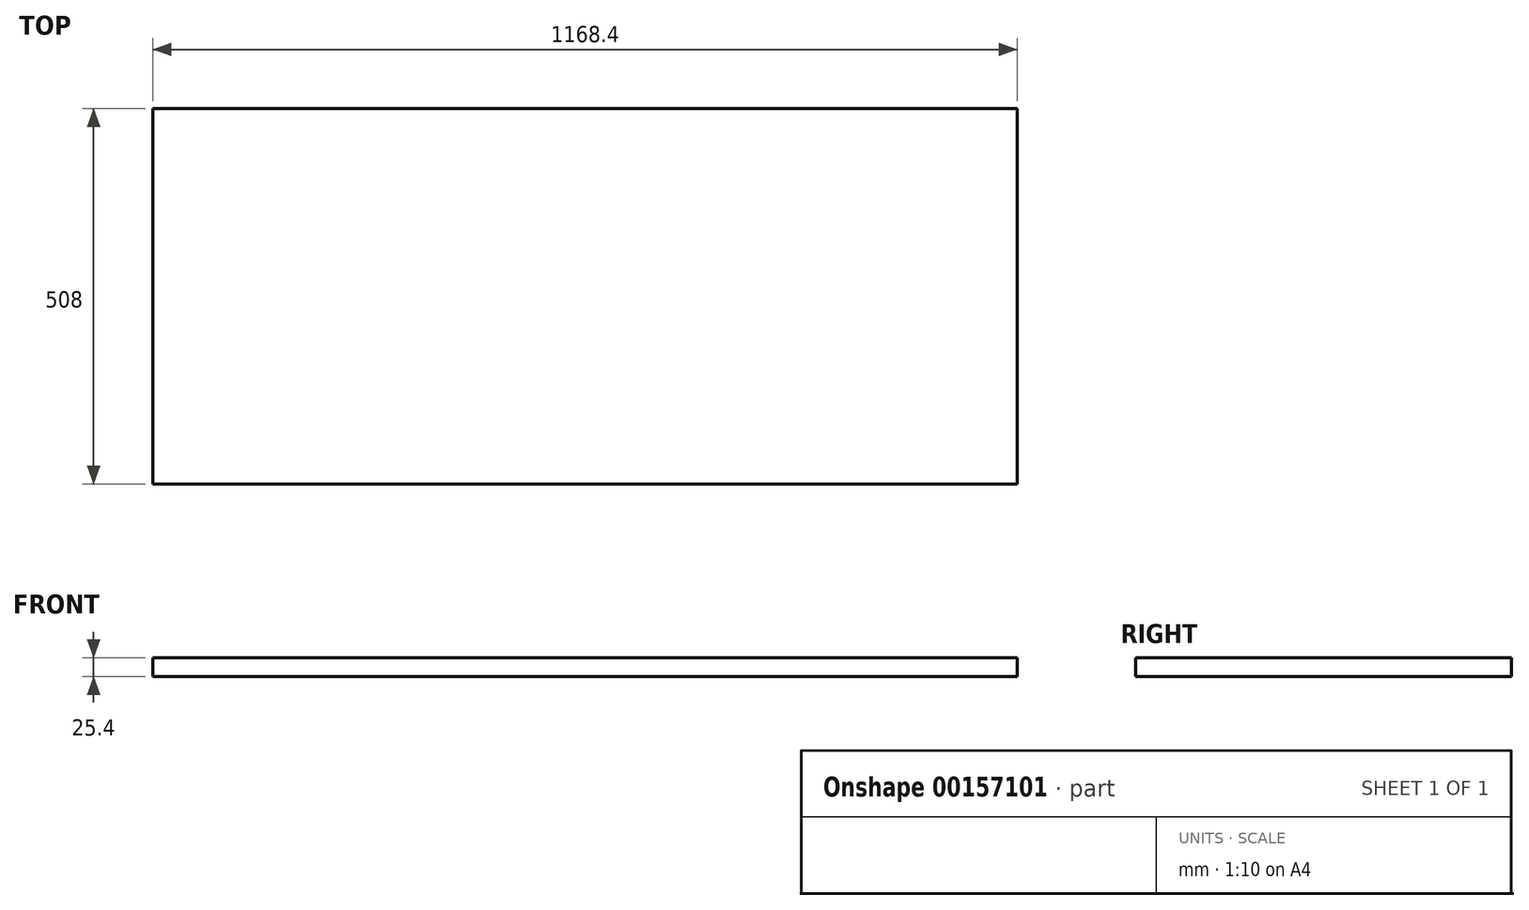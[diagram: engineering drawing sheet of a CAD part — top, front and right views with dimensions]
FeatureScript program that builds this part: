
annotation { "Feature Type Name" : "Feature", "Feature Type Description" : "" }
export const myFeature = defineFeature(function(context is Context, id is Id, definition is map)
    precondition{}
    {
        {
            var Q0;
            Q0=qCreatedBy(makeId("Top.planeOp"),FACE);
            var sketch = newSketch(context, id + "F0", { "sketchPlane" : qUnion([Q0])});
            skLineSegment(sketch, "E0.bottom", {"start": v(584.2, 254) * mm, "end": v(-584.2, 254) * mm});
            skLineSegment(sketch, "E0.top", {"start": v(584.2, -254) * mm, "end": v(-584.2, -254) * mm});
            skLineSegment(sketch, "E0.left", {"start": v(584.2, 254) * mm, "end": v(584.2, -254) * mm});
            skLineSegment(sketch, "E0.right", {"start": v(-584.2, 254) * mm, "end": v(-584.2, -254) * mm});
            skPoint(sketch, "E0.middle", {"position": v(0, 0) * mm});
            skSolve(sketch);
        }
        {
            var Q0;
            Q0 = qSketchRegion(id + "F0", true);
            extrude(context, id + "F1", {"entities" : qUnion([Q0]), "depth" : 25.4 * mm});
        }
    });
